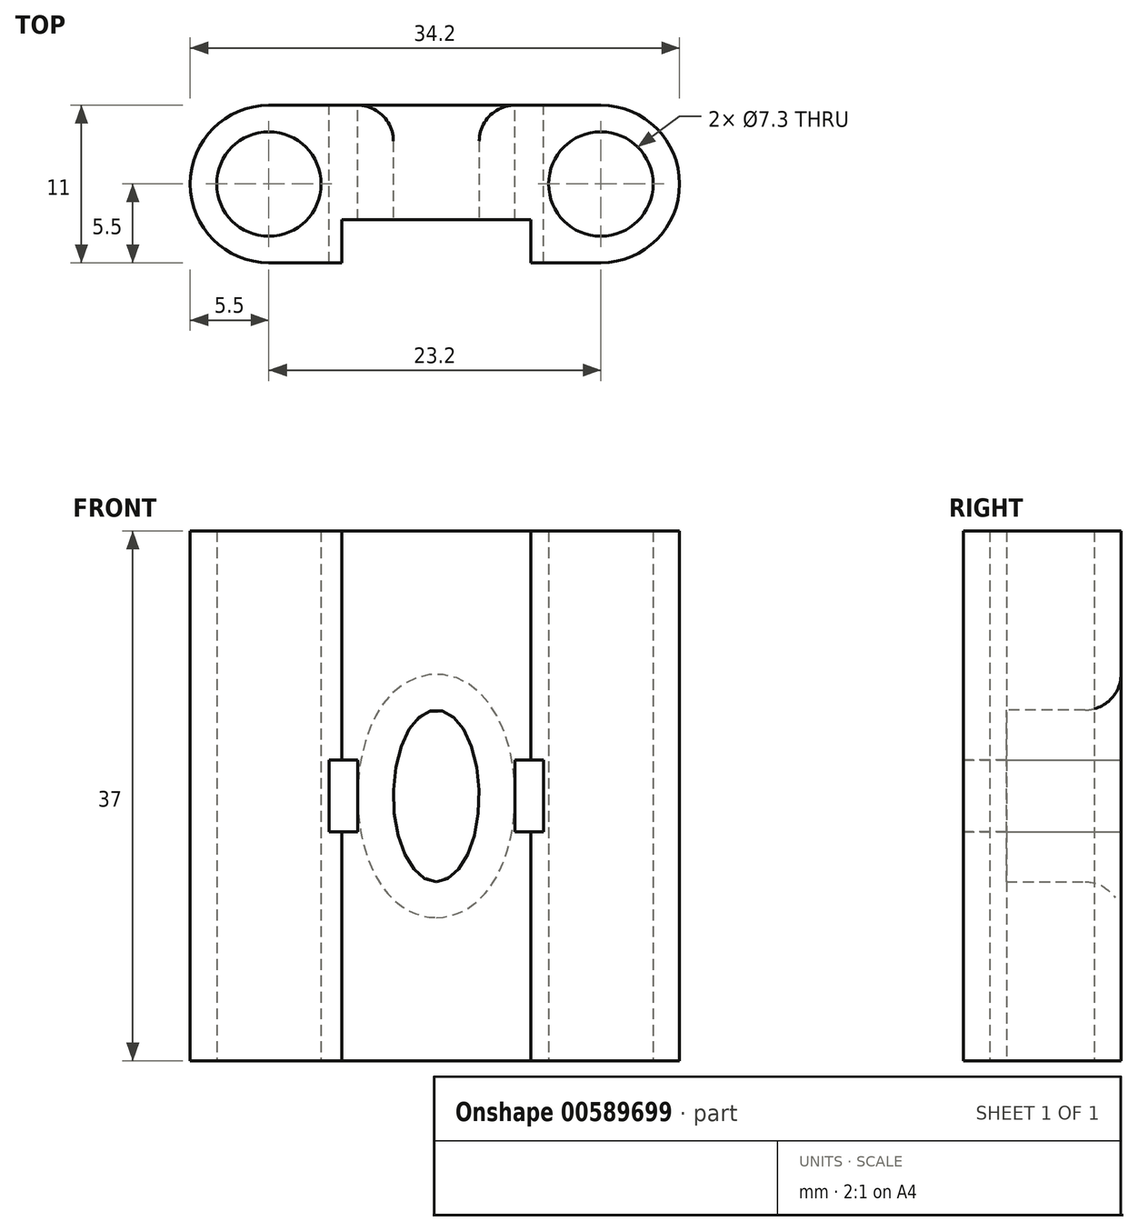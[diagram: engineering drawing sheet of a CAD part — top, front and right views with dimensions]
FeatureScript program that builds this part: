
annotation { "Feature Type Name" : "Feature", "Feature Type Description" : "" }
export const myFeature = defineFeature(function(context is Context, id is Id, definition is map)
    precondition{}
    {
        {
            var Q0;
            Q0=qCreatedBy(makeId("Top.planeOp"),FACE);
            var sketch = newSketch(context, id + "F0", { "sketchPlane" : qUnion([Q0])});
            skCircle(sketch, "E0", {"center": v(-11.7, 0) * mm, "radius": 3.65 * mm});
            skCircle(sketch, "E1", {"center": v(11.5, 0) * mm, "radius": 3.65 * mm});
            skArc(sketch, "E2", {"start": v(-11.7, 5.5) * mm, "mid": v(-17.2, 0) * mm, "end": v(-11.7, -5.5) * mm});
            skArc(sketch, "E3", {"start": v(11.5, -5.5) * mm, "mid": v(17, 0) * mm, "end": v(11.5, 5.5) * mm});
            skLineSegment(sketch, "E4", {"start": v(-11.7, 5.5) * mm, "end": v(11.5, 5.5) * mm});
            skLineSegment(sketch, "E5", {"start": v(11.5, -5.5) * mm, "end": v(6.6, -5.5) * mm});
            skLineSegment(sketch, "E6.bottom", {"start": v(-6.6, -2.5) * mm, "end": v(6.6, -2.5) * mm});
            skLineSegment(sketch, "E6.left", {"start": v(-6.6, -2.5) * mm, "end": v(-6.6, -5.5) * mm});
            skLineSegment(sketch, "E6.right", {"start": v(6.6, -2.5) * mm, "end": v(6.6, -5.5) * mm});
            skLineSegment(sketch, "E7.trimOffspring", {"start": v(-6.6, -5.5) * mm, "end": v(-11.7, -5.5) * mm});
            skSolve(sketch);
        }
        {
            var Q0;
            Q0 = qSketchRegion(id + "F0", true);
            extrude(context, id + "F1", {"entities" : qUnion([Q0]), "depth" : 37 * mm, "offsetDistance" : 25 * mm});
        }
        {
            var Q0;
            Q0=qCreatedBy(makeId("Front.planeOp"),FACE);
            var sketch = newSketch(context, id + "F2", { "sketchPlane" : qUnion([Q0])});
            skLineSegment(sketch, "E8.bottom", {"start": v(-7.5, 21) * mm, "end": v(-5.5, 21) * mm});
            skLineSegment(sketch, "E8.top", {"start": v(-7.5, 16) * mm, "end": v(-5.5, 16) * mm});
            skLineSegment(sketch, "E8.left", {"start": v(-7.5, 21) * mm, "end": v(-7.5, 16) * mm});
            skLineSegment(sketch, "E8.right", {"start": v(-5.5, 21) * mm, "end": v(-5.5, 16) * mm});
            skLineSegment(sketch, "E9.bottom", {"start": v(5.5, 21) * mm, "end": v(7.5, 21) * mm});
            skLineSegment(sketch, "E9.top", {"start": v(5.5, 16) * mm, "end": v(7.5, 16) * mm});
            skLineSegment(sketch, "E9.left", {"start": v(5.5, 21) * mm, "end": v(5.5, 16) * mm});
            skLineSegment(sketch, "E9.right", {"start": v(7.5, 21) * mm, "end": v(7.5, 16) * mm});
            skEllipse(sketch, "E10", {"center": v(0, 18.5) * mm, "majorRadius": 6 * mm, "minorRadius": 3 * mm, "majorAxis": v(0, -1)});
            skSolve(sketch);
        }
        {
            var Q0;
            Q0 = qSketchRegion(id + "F2", true);
            extrude(context, id + "F3", {"entities" : qUnion([Q0]), "operationType" : NewBodyOperationType.REMOVE, "oppositeDirection" : true, "depth" : -20 * mm, "offsetDistance" : 25 * mm, "hasSecondDirection" : true, "secondDirectionOppositeDirection" : true, "secondDirectionDepth" : 20 * mm});
        }
        {
            var Q0;
            Q0=makeQuery(id+"F3.boolean.opBoolean","INTERSECT",EDGE,{"derivedFrom":[makeQuery(id+"F1.opExtrude","SWEPT_FACE",FACE,{"disambiguationData":[OSD([sQuery(id+"F0.wireOp",EDGE,"E4")])]}),makeQuery(id+"F3.opExtrude","SWEPT_FACE",FACE,{"disambiguationData":[OSD([sQuery(id+"F2.wireOp",EDGE,"E10")])]})]});
            fillet(context, id + "F4", {"entities" : qUnion([Q0]), "radius" : 2.5 * mm, "tangentPropagation" : true, "allowEdgeOverflow" : false});
        }
    });
